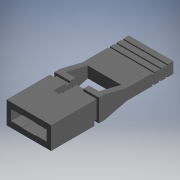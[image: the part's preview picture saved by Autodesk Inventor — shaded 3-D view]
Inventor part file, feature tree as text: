
AUTODESK INVENTOR PART (.ipt)
format: ipt  version: 2017.3 (Build 213256000, 256)  size: 196,096 bytes
history: native  units: mm (DEFAULTED — no unit token found)
features: extrude x9, sketch x9
ambient origin geometry x8: Origin, YZ Plane, XZ Plane, XY Plane, X Axis, Y Axis, Z Axis, Center Point
bodies: Solid1 (feature_tree), body_to_dummy_XY (feature_tree), body_to_dummy_YZ (feature_tree), body_to_dummy_ZX (feature_tree), body_to_dummy_X (feature_tree), body_to_dummy_Y (feature_tree), body_to_dummy_Z (feature_tree), body_to_dummy_Center (feature_tree)
feature tree (18):
  extrude  "Extrusion1"  Depth=0.508mm TaperAngle=0.0deg
  extrude  "Extrusion2"  Depth=6.096mm TaperAngle=0.0deg
  extrude  "Extrusion3"  Depth=3.556mm TaperAngle=0.0deg
  extrude  "Extrusion4"  Depth=5.08mm TaperAngle=0.0deg
  extrude  "Extrusion5"  TaperAngle=0.0deg  [1 undecoded]
  extrude  "Extrusion6"  [1 undecoded]
  extrude  "Extrusion7"  [1 undecoded]
  extrude  "Extrusion8"  [1 undecoded]
  extrude  "Extrusion9"  [1 undecoded]
  sketch  "Sketch_1"  dims[d0=6.096mm d1=0.0mm d2=0.508mm d3=0.0mm]
  sketch  "Sketch_2"  dims[d4=2.54mm d5=0.0mm d6=6.096mm d7=0.0mm]
  sketch  "Sketch_3"  dims[d8=6.096mm d9=0.0mm d10=3.556mm d11=0.0mm]
  sketch  "Sketch_4"  dims[d12=1.27mm d13=0.0mm d14=5.08mm d15=0.0mm]
  sketch  "Sketch_5"  dims[d16=3.81mm d17=0.0mm d18=0.0mm]
  sketch  "Sketch_8"
  sketch  "Sketch_6"
  sketch  "Sketch_7"
  sketch  "Sketch_10"
note: 5 required parameter values undecoded (feature->parameter linkage not recoverable at this tier; creation-order binding heuristic only, values carry confidence <= 0.55)
